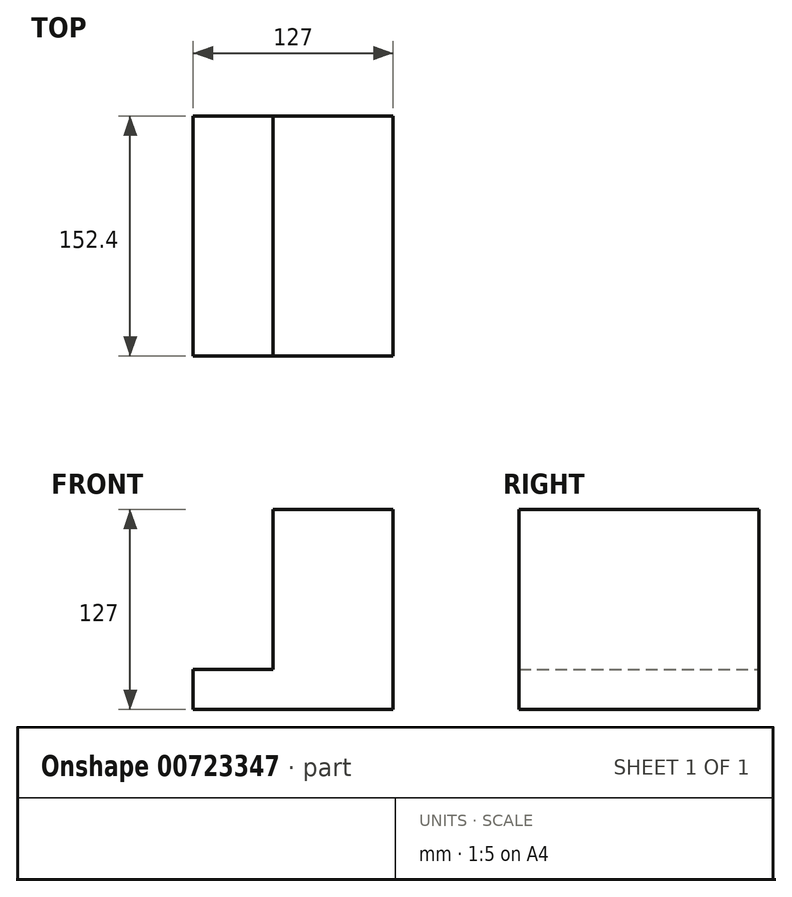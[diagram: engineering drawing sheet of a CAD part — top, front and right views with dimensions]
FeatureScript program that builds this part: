
annotation { "Feature Type Name" : "Feature", "Feature Type Description" : "" }
export const myFeature = defineFeature(function(context is Context, id is Id, definition is map)
    precondition{}
    {
        {
            var Q0;
            Q0=qCreatedBy(makeId("Front.planeOp"),FACE);
            var sketch = newSketch(context, id + "F0", { "sketchPlane" : qUnion([Q0])});
            skLineSegment(sketch, "E0", {"start": v(-85.66, -54.51) * mm, "end": v(41.34, -54.51) * mm});
            skLineSegment(sketch, "E1", {"start": v(-85.66, -54.51) * mm, "end": v(-85.66, -29.11) * mm});
            skLineSegment(sketch, "E2", {"start": v(-85.66, -29.11) * mm, "end": v(-34.86, -29.11) * mm});
            skLineSegment(sketch, "E3", {"start": v(-34.86, -29.11) * mm, "end": v(-34.86, 72.49) * mm});
            skLineSegment(sketch, "E4", {"start": v(-34.86, 72.49) * mm, "end": v(41.34, 72.49) * mm});
            skLineSegment(sketch, "E5", {"start": v(41.34, 72.49) * mm, "end": v(41.34, -54.51) * mm});
            skSolve(sketch);
        }
        {
            var Q0;
            Q0=makeQuery(id+"F0.imprint","IMPRINT",FACE,{"disambiguationData":[TD([[makeQuery(id+"F0.imprint","IMPRINT",EDGE,{"derivedFrom":sQuery(id+"F0.wireOp",EDGE,"E0")}),1.0]])]});
            extrude(context, id + "F1", {"entities" : qUnion([Q0]), "depth" : 152.4 * mm, "offsetDistance" : 25.4 * mm});
        }
    });
